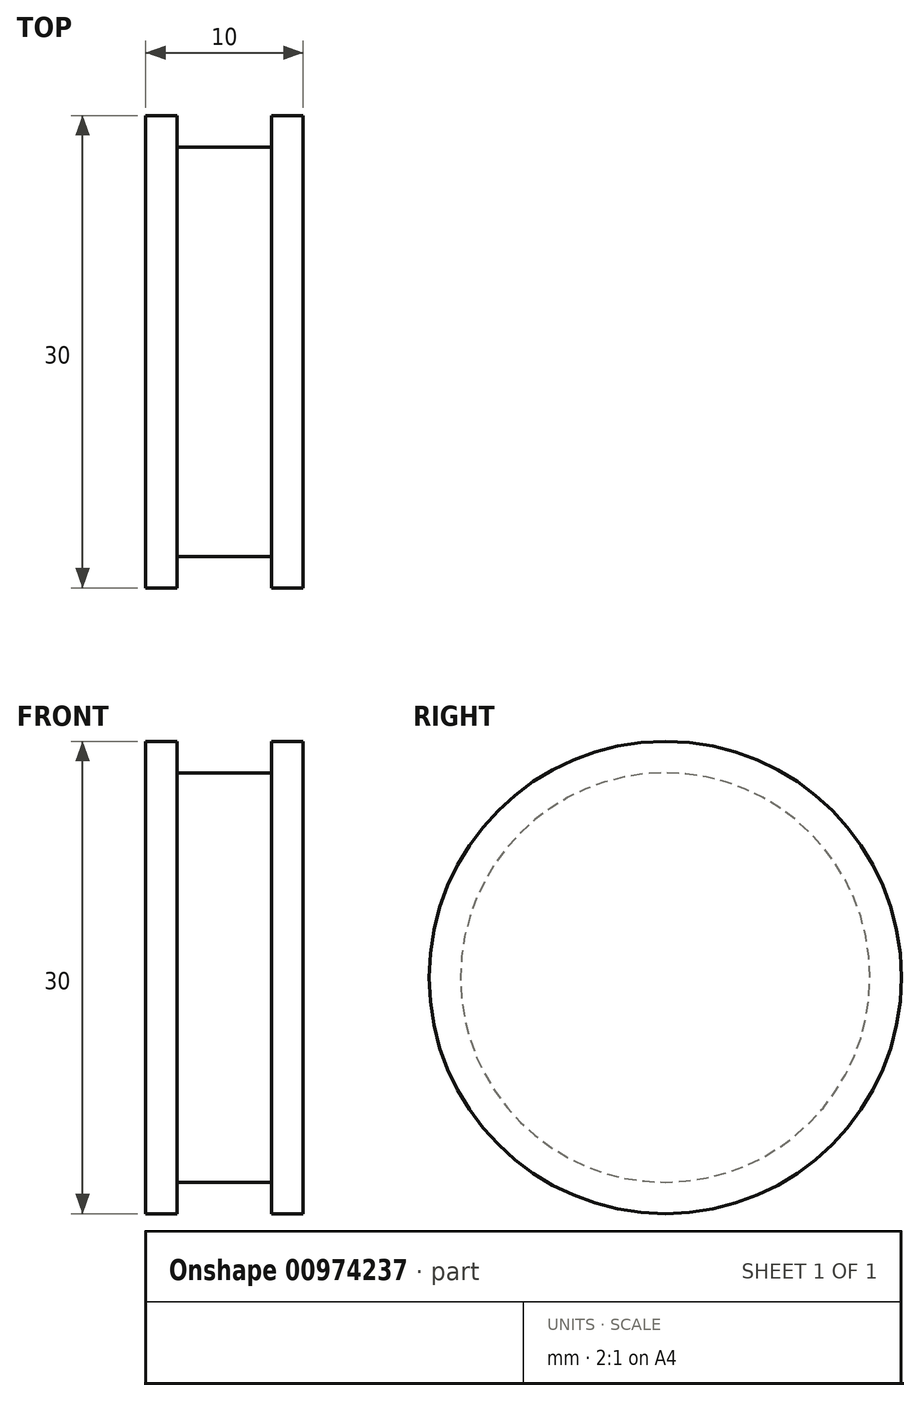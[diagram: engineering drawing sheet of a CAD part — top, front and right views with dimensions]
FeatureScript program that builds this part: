
annotation { "Feature Type Name" : "Feature", "Feature Type Description" : "" }
export const myFeature = defineFeature(function(context is Context, id is Id, definition is map)
    precondition{}
    {
        {
            var Q0;
            Q0=qCreatedBy(makeId("Right.planeOp"),FACE);
            var sketch = newSketch(context, id + "F0", { "sketchPlane" : qUnion([Q0])});
            skCircle(sketch, "E0", {"center": v(0, 0) * mm, "radius": 15 * mm});
            skSolve(sketch);
        }
        {
            var Q0;
            Q0 = qSketchRegion(id + "F0", true);
            var Q1;
            Q1 = qSketchRegion(id + "F2", true);
            extrude(context, id + "F1", {"entities" : qUnion([Q0, Q1]), "endBound" : BoundingType.SYMMETRIC, "depth" : 10 * mm, "offsetDistance" : 25 * mm});
        }
        {
            var Q0;
            Q0=qCreatedBy(makeId("Right.planeOp"),FACE);
            var sketch = newSketch(context, id + "F2", { "sketchPlane" : qUnion([Q0])});
            skCircle(sketch, "E1", {"center": v(0, 0) * mm, "radius": 13 * mm});
            skCircle(sketch, "E2", {"center": v(0, 0) * mm, "radius": 15 * mm});
            skSolve(sketch);
        }
        {
            var Q0;
            Q0 = qSketchRegion(id + "F2", true);
            extrude(context, id + "F3", {"entities" : qUnion([Q0]), "operationType" : NewBodyOperationType.REMOVE, "endBound" : BoundingType.SYMMETRIC, "oppositeDirection" : true, "depth" : 6 * mm, "offsetDistance" : 25 * mm});
        }
    });
